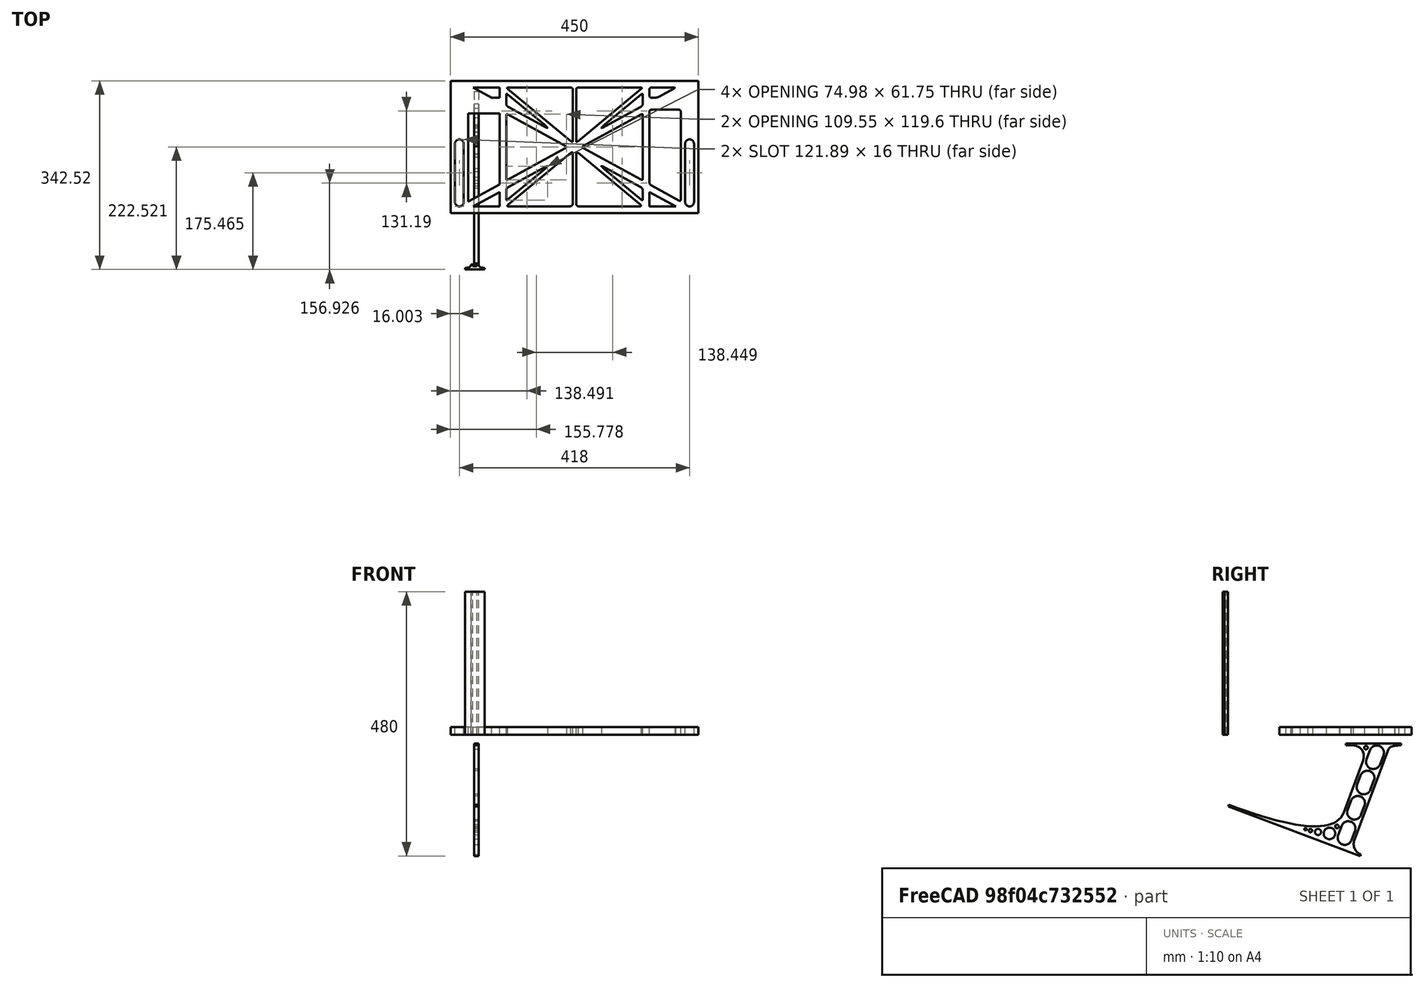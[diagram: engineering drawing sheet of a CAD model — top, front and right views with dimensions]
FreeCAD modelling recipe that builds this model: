
FCSTD DOCUMENT  (FreeCAD 0.19R0.19.2)
Label: laptopStand110
License: All rights reserved
LicenseURL: http://en.wikipedia.org/wiki/All_rights_reserved
objects: Sketcher::SketchObject×3, Part::Extrusion×3
note: 6 computed .brp shape members not serialized (recipe doc carries the construction recipe); baked Part::Feature solids carry a one-line shape summary decoded from their .brp

FEATURE [Sketcher::SketchObject] Sketch
  FullyConstrained = false
  sketch-geometry (298):
    g0: LineSegment StartX=-10.9272 StartY=-82.7794 StartZ=0 EndX=46.0728 EndY=-51.4823 EndZ=0
    g1: LineSegment StartX=-10.9272 StartY=77.3346 StartZ=0 EndX=-10.9272 EndY=-82.7794 EndZ=0
    g2: LineSegment StartX=-1.92719 StartY=-91.7794 StartZ=0 EndX=46.0728 EndY=-91.7794 EndZ=0
    g3: LineSegment StartX=318.073 StartY=-65.424 StartZ=0 EndX=318.073 EndY=-91.7794 EndZ=0
    g4: LineSegment StartX=318.073 StartY=-91.7794 StartZ=0 EndX=366.073 EndY=-91.7794 EndZ=0
    g5: LineSegment StartX=46.0728 StartY=-65.424 StartZ=0 EndX=-1.92719 EndY=-91.7794 EndZ=0
    g6: LineSegment StartX=46.0728 StartY=-65.424 StartZ=0 EndX=46.0728 EndY=-91.7794 EndZ=0
    g7: LineSegment StartX=46.0728 StartY=77.3346 StartZ=0 EndX=46.0728 EndY=-51.4823 EndZ=0
    g8: LineSegment StartX=-42.9272 StartY=136.221 StartZ=0 EndX=-42.9272 EndY=-103.779 EndZ=0
    g9: LineSegment StartX=407.073 StartY=136.221 StartZ=0 EndX=407.073 EndY=-103.779 EndZ=0
    g10: ArcOfCircle CenterX=-26.9272 CenterY=22.1087 CenterZ=0 NormalX=0 NormalY=0 NormalZ=1 AngleXU=0 Radius=8 StartAngle=1e-16 EndAngle=3.14159
    g11: ArcOfCircle CenterX=-26.9272 CenterY=-83.7794 CenterZ=0 NormalX=0 NormalY=0 NormalZ=1 AngleXU=0 Radius=8 StartAngle=3.14159 EndAngle=6.28319
    g12: LineSegment StartX=-34.9272 StartY=22.1087 StartZ=0 EndX=-34.9272 EndY=-83.7794 EndZ=0
    g13: LineSegment StartX=-18.9272 StartY=22.1087 StartZ=0 EndX=-18.9272 EndY=-83.7794 EndZ=0
    g14: ArcOfCircle CenterX=391.073 CenterY=22.1087 CenterZ=0 NormalX=0 NormalY=0 NormalZ=1 AngleXU=0 Radius=8 StartAngle=-4.4e-15 EndAngle=3.14159
    g15: LineSegment StartX=399.073 StartY=22.1087 StartZ=0 EndX=399.073 EndY=-83.7794 EndZ=0
    g16: LineSegment StartX=383.073 StartY=22.1087 StartZ=0 EndX=383.073 EndY=-83.7794 EndZ=0
    g17: ArcOfCircle CenterX=391.073 CenterY=-83.7794 CenterZ=0 NormalX=0 NormalY=0 NormalZ=1 AngleXU=0 Radius=8 StartAngle=3.14159 EndAngle=6.28319
    g18: Circle CenterX=175.022 CenterY=27.0628 CenterZ=0 NormalX=0 NormalY=0 NormalZ=1 AngleXU=0 Radius=1
    g19: Circle CenterX=179.022 CenterY=24.8665 CenterZ=0 NormalX=0 NormalY=0 NormalZ=1 AngleXU=0 Radius=1
    g20: Circle CenterX=179.022 CenterY=27.0628 CenterZ=0 NormalX=0 NormalY=0 NormalZ=1 AngleXU=0 Radius=1
    g21: BSplineCurve PolesCount=3 KnotsCount=2 Degree=2 IsPeriodic=0
    g22: GeomPoint X=175.022 Y=27.0628 Z=0
    g23: GeomPoint X=179.022 Y=27.0628 Z=0
    g24: Circle CenterX=189.124 CenterY=27.0628 CenterZ=0 NormalX=0 NormalY=0 NormalZ=1 AngleXU=0 Radius=1
    g25: Circle CenterX=185.124 CenterY=24.8665 CenterZ=0 NormalX=0 NormalY=0 NormalZ=1 AngleXU=0 Radius=1
    g26: Circle CenterX=185.124 CenterY=27.0628 CenterZ=0 NormalX=0 NormalY=0 NormalZ=1 AngleXU=0 Radius=1
    g27: BSplineCurve PolesCount=3 KnotsCount=2 Degree=2 IsPeriodic=0
    g28: GeomPoint X=189.124 Y=27.0628 Z=0
    g29: GeomPoint X=185.124 Y=27.0628 Z=0
    g30: Circle CenterX=175.022 CenterY=5.37834 CenterZ=0 NormalX=0 NormalY=0 NormalZ=1 AngleXU=0 Radius=1
    g31: Circle CenterX=179.022 CenterY=7.57463 CenterZ=0 NormalX=0 NormalY=0 NormalZ=1 AngleXU=0 Radius=1
    g32: Circle CenterX=179.022 CenterY=5.34704 CenterZ=0 NormalX=0 NormalY=0 NormalZ=1 AngleXU=0 Radius=1
    g33: BSplineCurve PolesCount=3 KnotsCount=2 Degree=2 IsPeriodic=0
    g34: GeomPoint X=175.022 Y=5.37834 Z=0
    g35: GeomPoint X=179.022 Y=5.34704 Z=0
    g36: Circle CenterX=189.124 CenterY=5.37834 CenterZ=0 NormalX=0 NormalY=0 NormalZ=1 AngleXU=0 Radius=1
    g37: Circle CenterX=185.124 CenterY=7.57463 CenterZ=0 NormalX=0 NormalY=0 NormalZ=1 AngleXU=0 Radius=1
    g38: Circle CenterX=185.124 CenterY=5.34704 CenterZ=0 NormalX=0 NormalY=0 NormalZ=1 AngleXU=0 Radius=1
    g39: BSplineCurve PolesCount=3 KnotsCount=2 Degree=2 IsPeriodic=0
    g40: GeomPoint X=189.124 Y=5.37834 Z=0
    g41: GeomPoint X=185.124 Y=5.34704 Z=0
    g42: Circle CenterX=165.871 CenterY=18.1458 CenterZ=0 NormalX=0 NormalY=0 NormalZ=1 AngleXU=0 Radius=1
    g43: Circle CenterX=169.377 CenterY=16.2206 CenterZ=0 NormalX=0 NormalY=0 NormalZ=1 AngleXU=0 Radius=1
    g44: Circle CenterX=165.871 CenterY=14.2954 CenterZ=0 NormalX=0 NormalY=0 NormalZ=1 AngleXU=0 Radius=1
    g45: BSplineCurve PolesCount=3 KnotsCount=2 Degree=2 IsPeriodic=0
    g46: GeomPoint X=165.871 Y=18.1458 Z=0
    g47: GeomPoint X=165.871 Y=14.2954 Z=0
    g48: Circle CenterX=198.275 CenterY=18.1458 CenterZ=0 NormalX=0 NormalY=0 NormalZ=1 AngleXU=0 Radius=1
    g49: Circle CenterX=194.768 CenterY=16.2206 CenterZ=0 NormalX=0 NormalY=0 NormalZ=1 AngleXU=0 Radius=1
    g50: Circle CenterX=198.275 CenterY=14.2954 CenterZ=0 NormalX=0 NormalY=0 NormalZ=1 AngleXU=0 Radius=1
    g51: BSplineCurve PolesCount=3 KnotsCount=2 Degree=2 IsPeriodic=0
    g52: GeomPoint X=198.275 Y=18.1458 Z=0
    g53: GeomPoint X=198.275 Y=14.2954 Z=0
    g54: LineSegment StartX=407.073 StartY=-103.779 StartZ=0 EndX=-42.9272 EndY=-103.779 EndZ=0
    g55: LineSegment StartX=407.073 StartY=136.221 StartZ=0 EndX=-42.9272 EndY=136.221 EndZ=0
    g56: LineSegment StartX=46.0728 StartY=77.3346 StartZ=0 EndX=-10.9272 EndY=77.3346 EndZ=0
    g57: LineSegment StartX=46.0728 StartY=105.865 StartZ=0 EndX=31.5028 EndY=105.865 EndZ=0
    g58: LineSegment StartX=46.0728 StartY=124.221 StartZ=0 EndX=46.0728 EndY=105.865 EndZ=0
    g59: LineSegment StartX=-1.92719 StartY=124.221 StartZ=0 EndX=31.5028 EndY=105.865 EndZ=0
    g60: LineSegment StartX=46.0728 StartY=124.221 StartZ=0 EndX=-1.92719 EndY=124.221 EndZ=0
    g61: Circle CenterX=125.607 CenterY=54.1951 CenterZ=0 NormalX=0 NormalY=0 NormalZ=1 AngleXU=0 Radius=1
    g62: Circle CenterX=139.632 CenterY=46.4944 CenterZ=0 NormalX=0 NormalY=0 NormalZ=1 AngleXU=0 Radius=1
    g63: Circle CenterX=127.326 CenterY=56.7187 CenterZ=0 NormalX=0 NormalY=0 NormalZ=1 AngleXU=0 Radius=1
    g64: BSplineCurve PolesCount=3 KnotsCount=2 Degree=2 IsPeriodic=0
    g65: GeomPoint X=125.607 Y=54.1951 Z=0
    g66: GeomPoint X=127.326 Y=56.7187 Z=0
    g67: Circle CenterX=236.821 CenterY=56.7187 CenterZ=0 NormalX=0 NormalY=0 NormalZ=1 AngleXU=0 Radius=1
    g68: Circle CenterX=224.513 CenterY=46.4944 CenterZ=0 NormalX=0 NormalY=0 NormalZ=1 AngleXU=0 Radius=1
    g69: Circle CenterX=238.538 CenterY=54.1951 CenterZ=0 NormalX=0 NormalY=0 NormalZ=1 AngleXU=0 Radius=1
    g70: BSplineCurve PolesCount=3 KnotsCount=2 Degree=2 IsPeriodic=0
    g71: GeomPoint X=236.821 Y=56.7187 Z=0
    g72: GeomPoint X=238.538 Y=54.1951 Z=0
    g73: Circle CenterX=238.538 CenterY=-21.7539 CenterZ=0 NormalX=0 NormalY=0 NormalZ=1 AngleXU=0 Radius=1
    g74: Circle CenterX=224.513 CenterY=-14.0532 CenterZ=0 NormalX=0 NormalY=0 NormalZ=1 AngleXU=0 Radius=1
    g75: Circle CenterX=236.821 CenterY=-24.2775 CenterZ=0 NormalX=0 NormalY=0 NormalZ=1 AngleXU=0 Radius=1
    g76: BSplineCurve PolesCount=3 KnotsCount=2 Degree=2 IsPeriodic=0
    g77: GeomPoint X=238.538 Y=-21.7539 Z=0
    g78: GeomPoint X=236.821 Y=-24.2775 Z=0
    g79: Circle CenterX=125.607 CenterY=-21.7539 CenterZ=0 NormalX=0 NormalY=0 NormalZ=1 AngleXU=0 Radius=1
    g80: Circle CenterX=139.632 CenterY=-14.0532 CenterZ=0 NormalX=0 NormalY=0 NormalZ=1 AngleXU=0 Radius=1
    g81: Circle CenterX=127.325 CenterY=-24.2775 CenterZ=0 NormalX=0 NormalY=0 NormalZ=1 AngleXU=0 Radius=1
    g82: BSplineCurve PolesCount=3 KnotsCount=2 Degree=2 IsPeriodic=0
    g83: GeomPoint X=125.607 Y=-21.7539 Z=0
    g84: GeomPoint X=127.325 Y=-24.2775 Z=0
    g85: Circle CenterX=302.996 CenterY=111.695 CenterZ=0 NormalX=0 NormalY=0 NormalZ=1 AngleXU=0 Radius=1
    g86: Circle CenterX=306.073 CenterY=114.251 CenterZ=0 NormalX=0 NormalY=0 NormalZ=1 AngleXU=0 Radius=1
    g87: Circle CenterX=306.073 CenterY=110.251 CenterZ=0 NormalX=0 NormalY=0 NormalZ=1 AngleXU=0 Radius=1
    g88: BSplineCurve PolesCount=3 KnotsCount=2 Degree=2 IsPeriodic=0
    g89: GeomPoint X=302.996 Y=111.695 Z=0
    g90: GeomPoint X=306.073 Y=110.251 Z=0
    g91: Circle CenterX=306.073 CenterY=95.2763 CenterZ=0 NormalX=0 NormalY=0 NormalZ=1 AngleXU=0 Radius=1
    g92: Circle CenterX=306.073 CenterY=91.2763 CenterZ=0 NormalX=0 NormalY=0 NormalZ=1 AngleXU=0 Radius=1
    g93: Circle CenterX=302.567 CenterY=89.3511 CenterZ=0 NormalX=0 NormalY=0 NormalZ=1 AngleXU=0 Radius=1
    g94: BSplineCurve PolesCount=3 KnotsCount=2 Degree=2 IsPeriodic=0
    g95: GeomPoint X=306.073 Y=95.2763 Z=0
    g96: GeomPoint X=302.567 Y=89.3511 Z=0
    g97: LineSegment StartX=306.073 StartY=110.251 StartZ=0 EndX=306.073 EndY=95.2763 EndZ=0
    g98: LineSegment StartX=302.996 StartY=111.695 StartZ=0 EndX=236.821 EndY=56.7187 EndZ=0
    g99: LineSegment StartX=238.538 StartY=54.1951 StartZ=0 EndX=302.567 EndY=89.3511 EndZ=0
    g100: Circle CenterX=61.1496 CenterY=111.695 CenterZ=0 NormalX=0 NormalY=0 NormalZ=1 AngleXU=0 Radius=1
    g101: Circle CenterX=58.0728 CenterY=114.251 CenterZ=0 NormalX=0 NormalY=0 NormalZ=1 AngleXU=0 Radius=1
    g102: Circle CenterX=58.0728 CenterY=110.251 CenterZ=0 NormalX=0 NormalY=0 NormalZ=1 AngleXU=0 Radius=1
    g103: BSplineCurve PolesCount=3 KnotsCount=2 Degree=2 IsPeriodic=0
    g104: GeomPoint X=61.1496 Y=111.695 Z=0
    g105: GeomPoint X=58.0728 Y=110.251 Z=0
    g106: Circle CenterX=61.5791 CenterY=89.3511 CenterZ=0 NormalX=0 NormalY=0 NormalZ=1 AngleXU=0 Radius=1
    g107: Circle CenterX=58.0728 CenterY=91.2763 CenterZ=0 NormalX=0 NormalY=0 NormalZ=1 AngleXU=0 Radius=1
    g108: Circle CenterX=58.0728 CenterY=95.2763 CenterZ=0 NormalX=0 NormalY=0 NormalZ=1 AngleXU=0 Radius=1
    g109: BSplineCurve PolesCount=3 KnotsCount=2 Degree=2 IsPeriodic=0
    g110: GeomPoint X=61.5791 Y=89.3511 Z=0
    g111: GeomPoint X=58.0728 Y=95.2763 Z=0
    g112: LineSegment StartX=58.0728 StartY=110.251 StartZ=0 EndX=58.0728 EndY=95.2763 EndZ=0
    g113: LineSegment StartX=61.1496 StartY=111.695 StartZ=0 EndX=127.326 EndY=56.7187 EndZ=0
    g114: LineSegment StartX=125.607 StartY=54.1951 StartZ=0 EndX=61.5791 EndY=89.3511 EndZ=0
    g115: Circle CenterX=61.5791 CenterY=-56.9099 CenterZ=0 NormalX=0 NormalY=0 NormalZ=1 AngleXU=0 Radius=1
    g116: Circle CenterX=58.0728 CenterY=-58.8351 CenterZ=0 NormalX=0 NormalY=0 NormalZ=1 AngleXU=0 Radius=1
    g117: Circle CenterX=58.0728 CenterY=-62.8351 CenterZ=0 NormalX=0 NormalY=0 NormalZ=1 AngleXU=0 Radius=1
    g118: BSplineCurve PolesCount=3 KnotsCount=2 Degree=2 IsPeriodic=0
    g119: GeomPoint X=61.5791 Y=-56.9099 Z=0
    g120: GeomPoint X=58.0728 Y=-62.8351 Z=0
    g121: Circle CenterX=58.0728 CenterY=-77.8102 CenterZ=0 NormalX=0 NormalY=0 NormalZ=1 AngleXU=0 Radius=1
    g122: Circle CenterX=58.0728 CenterY=-81.8102 CenterZ=0 NormalX=0 NormalY=0 NormalZ=1 AngleXU=0 Radius=1
    g123: Circle CenterX=61.1496 CenterY=-79.2541 CenterZ=0 NormalX=0 NormalY=0 NormalZ=1 AngleXU=0 Radius=1
    g124: BSplineCurve PolesCount=3 KnotsCount=2 Degree=2 IsPeriodic=0
    g125: GeomPoint X=58.0728 Y=-77.8102 Z=0
    g126: GeomPoint X=61.1496 Y=-79.2541 Z=0
    g127: LineSegment StartX=58.0728 StartY=-62.8351 StartZ=0 EndX=58.0728 EndY=-77.8102 EndZ=0
    g128: LineSegment StartX=61.1496 StartY=-79.2541 StartZ=0 EndX=127.325 EndY=-24.2775 EndZ=0
    g129: LineSegment StartX=125.607 StartY=-21.7539 StartZ=0 EndX=61.5791 EndY=-56.9099 EndZ=0
    g130: Circle CenterX=302.567 CenterY=-56.9099 CenterZ=0 NormalX=0 NormalY=0 NormalZ=1 AngleXU=0 Radius=1
    g131: Circle CenterX=306.073 CenterY=-58.8351 CenterZ=0 NormalX=0 NormalY=0 NormalZ=1 AngleXU=0 Radius=1
    g132: Circle CenterX=306.073 CenterY=-62.8351 CenterZ=0 NormalX=0 NormalY=0 NormalZ=1 AngleXU=0 Radius=1
    g133: BSplineCurve PolesCount=3 KnotsCount=2 Degree=2 IsPeriodic=0
    g134: GeomPoint X=302.567 Y=-56.9099 Z=0
    g135: GeomPoint X=306.073 Y=-62.8351 Z=0
    g136: Circle CenterX=302.996 CenterY=-79.2541 CenterZ=0 NormalX=0 NormalY=0 NormalZ=1 AngleXU=0 Radius=1
    g137: Circle CenterX=306.073 CenterY=-81.8102 CenterZ=0 NormalX=0 NormalY=0 NormalZ=1 AngleXU=0 Radius=1
    g138: Circle CenterX=306.073 CenterY=-77.8102 CenterZ=0 NormalX=0 NormalY=0 NormalZ=1 AngleXU=0 Radius=1
    g139: BSplineCurve PolesCount=3 KnotsCount=2 Degree=2 IsPeriodic=0
    g140: GeomPoint X=302.996 Y=-79.2541 Z=0
    g141: GeomPoint X=306.073 Y=-77.8102 Z=0
    g142: LineSegment StartX=306.073 StartY=-62.8351 StartZ=0 EndX=306.073 EndY=-77.8102 EndZ=0
    g143: LineSegment StartX=302.996 StartY=-79.2541 StartZ=0 EndX=236.821 EndY=-24.2775 EndZ=0
    g144: LineSegment StartX=238.538 StartY=-21.7539 StartZ=0 EndX=302.567 EndY=-56.9099 EndZ=0
    g145: Circle CenterX=61.6457 CenterY=-88.8112 CenterZ=0 NormalX=0 NormalY=0 NormalZ=1 AngleXU=0 Radius=1
    g146: Circle CenterX=58.0728 CenterY=-91.7794 CenterZ=0 NormalX=0 NormalY=0 NormalZ=1 AngleXU=0 Radius=1
    g147: Circle CenterX=63.9135 CenterY=-91.7794 CenterZ=0 NormalX=0 NormalY=0 NormalZ=1 AngleXU=0 Radius=1
    g148: BSplineCurve PolesCount=3 KnotsCount=2 Degree=2 IsPeriodic=0
    g149: GeomPoint X=61.6457 Y=-88.8112 Z=0
    g150: GeomPoint X=63.9135 Y=-91.7794 Z=0
    g151: Circle CenterX=179.022 CenterY=-85.8163 CenterZ=0 NormalX=0 NormalY=0 NormalZ=1 AngleXU=0 Radius=1
    g152: Circle CenterX=179.022 CenterY=-91.7794 CenterZ=0 NormalX=0 NormalY=0 NormalZ=1 AngleXU=0 Radius=1
    g153: Circle CenterX=171.895 CenterY=-91.7794 CenterZ=0 NormalX=0 NormalY=0 NormalZ=1 AngleXU=0 Radius=1
    g154: BSplineCurve PolesCount=3 KnotsCount=2 Degree=2 IsPeriodic=0
    g155: GeomPoint X=179.022 Y=-85.8163 Z=0
    g156: GeomPoint X=171.895 Y=-91.7794 Z=0
    g157: Circle CenterX=185.124 CenterY=-86.2028 CenterZ=0 NormalX=0 NormalY=0 NormalZ=1 AngleXU=0 Radius=1
    g158: Circle CenterX=185.124 CenterY=-91.7794 CenterZ=0 NormalX=0 NormalY=0 NormalZ=1 AngleXU=0 Radius=1
    g159: Circle CenterX=191.747 CenterY=-91.7794 CenterZ=0 NormalX=0 NormalY=0 NormalZ=1 AngleXU=0 Radius=1
    g160: BSplineCurve PolesCount=3 KnotsCount=2 Degree=2 IsPeriodic=0
    g161: GeomPoint X=185.124 Y=-86.2028 Z=0
    g162: GeomPoint X=191.747 Y=-91.7794 Z=0
    g163: Circle CenterX=299.888 CenterY=-86.6413 CenterZ=0 NormalX=0 NormalY=0 NormalZ=1 AngleXU=0 Radius=1
    g164: Circle CenterX=306.073 CenterY=-91.7794 CenterZ=0 NormalX=0 NormalY=0 NormalZ=1 AngleXU=0 Radius=1
    g165: Circle CenterX=298.776 CenterY=-91.7794 CenterZ=0 NormalX=0 NormalY=0 NormalZ=1 AngleXU=0 Radius=1
    g166: BSplineCurve PolesCount=3 KnotsCount=2 Degree=2 IsPeriodic=0
    g167: GeomPoint X=299.888 Y=-86.6413 Z=0
    g168: GeomPoint X=298.776 Y=-91.7794 Z=0
    g169: LineSegment StartX=189.124 StartY=5.37834 StartZ=0 EndX=299.888 EndY=-86.6413 EndZ=0
    g170: LineSegment StartX=298.776 StartY=-91.7794 StartZ=0 EndX=191.747 EndY=-91.7794 EndZ=0
    g171: LineSegment StartX=185.124 StartY=-86.2028 StartZ=0 EndX=185.124 EndY=5.34704 EndZ=0
    g172: LineSegment StartX=179.022 StartY=5.34704 StartZ=0 EndX=179.022 EndY=-85.8163 EndZ=0
    g173: LineSegment StartX=171.895 StartY=-91.7794 StartZ=0 EndX=63.9135 EndY=-91.7794 EndZ=0
    g174: LineSegment StartX=61.6457 StartY=-88.8112 StartZ=0 EndX=175.022 EndY=5.37834 EndZ=0
    g175: Circle CenterX=302.073 CenterY=124.221 CenterZ=0 NormalX=0 NormalY=0 NormalZ=1 AngleXU=0 Radius=1
    g176: Circle CenterX=306.073 CenterY=124.221 CenterZ=0 NormalX=0 NormalY=0 NormalZ=1 AngleXU=0 Radius=1
    g177: Circle CenterX=302.996 CenterY=121.665 CenterZ=0 NormalX=0 NormalY=0 NormalZ=1 AngleXU=0 Radius=1
    g178: BSplineCurve PolesCount=3 KnotsCount=2 Degree=2 IsPeriodic=0
    g179: GeomPoint X=302.073 Y=124.221 Z=0
    g180: GeomPoint X=302.996 Y=121.665 Z=0
    g181: Circle CenterX=189.124 CenterY=124.221 CenterZ=0 NormalX=0 NormalY=0 NormalZ=1 AngleXU=0 Radius=1
    g182: Circle CenterX=185.124 CenterY=124.221 CenterZ=0 NormalX=0 NormalY=0 NormalZ=1 AngleXU=0 Radius=1
    g183: Circle CenterX=185.124 CenterY=120.221 CenterZ=0 NormalX=0 NormalY=0 NormalZ=1 AngleXU=0 Radius=1
    g184: BSplineCurve PolesCount=3 KnotsCount=2 Degree=2 IsPeriodic=0
    g185: GeomPoint X=189.124 Y=124.221 Z=0
    g186: GeomPoint X=185.124 Y=120.221 Z=0
    g187: Circle CenterX=175.022 CenterY=124.221 CenterZ=0 NormalX=0 NormalY=0 NormalZ=1 AngleXU=0 Radius=1
    g188: Circle CenterX=179.022 CenterY=124.221 CenterZ=0 NormalX=0 NormalY=0 NormalZ=1 AngleXU=0 Radius=1
    g189: Circle CenterX=179.022 CenterY=120.221 CenterZ=0 NormalX=0 NormalY=0 NormalZ=1 AngleXU=0 Radius=1
    g190: BSplineCurve PolesCount=3 KnotsCount=2 Degree=2 IsPeriodic=0
    g191: GeomPoint X=175.022 Y=124.221 Z=0
    g192: GeomPoint X=179.022 Y=120.221 Z=0
    g193: Circle CenterX=62.0728 CenterY=124.221 CenterZ=0 NormalX=0 NormalY=0 NormalZ=1 AngleXU=0 Radius=1
    g194: Circle CenterX=58.0728 CenterY=124.221 CenterZ=0 NormalX=0 NormalY=0 NormalZ=1 AngleXU=0 Radius=1
    g195: Circle CenterX=61.1496 CenterY=121.665 CenterZ=0 NormalX=0 NormalY=0 NormalZ=1 AngleXU=0 Radius=1
    g196: BSplineCurve PolesCount=3 KnotsCount=2 Degree=2 IsPeriodic=0
    g197: GeomPoint X=62.0728 Y=124.221 Z=0
    g198: GeomPoint X=61.1496 Y=121.665 Z=0
    g199: LineSegment StartX=62.0728 StartY=124.221 StartZ=0 EndX=175.022 EndY=124.221 EndZ=0
    g200: LineSegment StartX=179.022 StartY=120.221 StartZ=0 EndX=179.022 EndY=27.0628 EndZ=0
    g201: LineSegment StartX=185.124 StartY=27.0628 StartZ=0 EndX=185.124 EndY=120.221 EndZ=0
    g202: LineSegment StartX=189.124 StartY=124.221 StartZ=0 EndX=302.073 EndY=124.221 EndZ=0
    g203: LineSegment StartX=302.996 StartY=121.665 StartZ=0 EndX=189.124 EndY=27.0628 EndZ=0
    g204: LineSegment StartX=175.022 StartY=27.0628 StartZ=0 EndX=61.1496 EndY=121.665 EndZ=0
    g205: Circle CenterX=61.5791 CenterY=75.4095 CenterZ=0 NormalX=0 NormalY=0 NormalZ=1 AngleXU=0 Radius=1
    g206: Circle CenterX=58.0728 CenterY=77.3346 CenterZ=0 NormalX=0 NormalY=0 NormalZ=1 AngleXU=0 Radius=1
    g207: Circle CenterX=58.0728 CenterY=73.3346 CenterZ=0 NormalX=0 NormalY=0 NormalZ=1 AngleXU=0 Radius=1
    g208: BSplineCurve PolesCount=3 KnotsCount=2 Degree=2 IsPeriodic=0
    g209: GeomPoint X=61.5791 Y=75.4095 Z=0
    g210: GeomPoint X=58.0728 Y=73.3346 Z=0
    g211: Circle CenterX=58.0728 CenterY=-40.8935 CenterZ=0 NormalX=0 NormalY=0 NormalZ=1 AngleXU=0 Radius=1
    g212: Circle CenterX=58.0728 CenterY=-44.8935 CenterZ=0 NormalX=0 NormalY=0 NormalZ=1 AngleXU=0 Radius=1
    g213: Circle CenterX=61.5791 CenterY=-42.9683 CenterZ=0 NormalX=0 NormalY=0 NormalZ=1 AngleXU=0 Radius=1
    g214: BSplineCurve PolesCount=3 KnotsCount=2 Degree=2 IsPeriodic=0
    g215: GeomPoint X=58.0728 Y=-40.8935 Z=0
    g216: GeomPoint X=61.5791 Y=-42.9683 Z=0
    g217: LineSegment StartX=61.5791 StartY=-42.9683 StartZ=0 EndX=165.871 EndY=14.2954 EndZ=0
    g218: LineSegment StartX=165.871 StartY=18.1458 StartZ=0 EndX=61.5791 EndY=75.4095 EndZ=0
    g219: LineSegment StartX=58.0728 StartY=73.3346 StartZ=0 EndX=58.0728 EndY=-40.8935 EndZ=0
    g220: Circle CenterX=302.567 CenterY=-42.9683 CenterZ=0 NormalX=0 NormalY=0 NormalZ=1 AngleXU=0 Radius=1
    g221: Circle CenterX=306.073 CenterY=-44.8935 CenterZ=0 NormalX=0 NormalY=0 NormalZ=1 AngleXU=0 Radius=1
    g222: Circle CenterX=306.073 CenterY=-40.8935 CenterZ=0 NormalX=0 NormalY=0 NormalZ=1 AngleXU=0 Radius=1
    g223: BSplineCurve PolesCount=3 KnotsCount=2 Degree=2 IsPeriodic=0
    g224: GeomPoint X=302.567 Y=-42.9683 Z=0
    g225: GeomPoint X=306.073 Y=-40.8935 Z=0
    g226: Circle CenterX=306.073 CenterY=73.3346 CenterZ=0 NormalX=0 NormalY=0 NormalZ=1 AngleXU=0 Radius=1
    g227: Circle CenterX=306.073 CenterY=77.3346 CenterZ=0 NormalX=0 NormalY=0 NormalZ=1 AngleXU=0 Radius=1
    g228: Circle CenterX=302.567 CenterY=75.4095 CenterZ=0 NormalX=0 NormalY=0 NormalZ=1 AngleXU=0 Radius=1
    g229: BSplineCurve PolesCount=3 KnotsCount=2 Degree=2 IsPeriodic=0
    g230: GeomPoint X=306.073 Y=73.3346 Z=0
    g231: GeomPoint X=302.567 Y=75.4095 Z=0
    g232: LineSegment StartX=302.567 StartY=-42.9683 StartZ=0 EndX=198.275 EndY=14.2954 EndZ=0
    g233: LineSegment StartX=198.275 StartY=18.1458 StartZ=0 EndX=302.567 EndY=75.4095 EndZ=0
    g234: LineSegment StartX=306.073 StartY=73.3346 StartZ=0 EndX=306.073 EndY=-40.8935 EndZ=0
    g235: LineSegment StartX=322.073 StartY=105.865 StartZ=0 EndX=328.643 EndY=105.865 EndZ=0
    g236: LineSegment StartX=318.073 StartY=120.221 StartZ=0 EndX=318.073 EndY=109.865 EndZ=0
    g237: LineSegment StartX=336.157 StartY=107.779 StartZ=0 EndX=362.567 EndY=122.294 EndZ=0
    g238: Circle CenterX=362.073 CenterY=124.221 CenterZ=0 NormalX=0 NormalY=0 NormalZ=1 AngleXU=0 Radius=1
    g239: Circle CenterX=366.073 CenterY=124.221 CenterZ=0 NormalX=0 NormalY=0 NormalZ=1 AngleXU=0 Radius=1
    g240: Circle CenterX=362.567 CenterY=122.294 CenterZ=0 NormalX=0 NormalY=0 NormalZ=1 AngleXU=0 Radius=1
    g241: BSplineCurve PolesCount=3 KnotsCount=2 Degree=2 IsPeriodic=0
    g242: GeomPoint X=362.073 Y=124.221 Z=0
    g243: GeomPoint X=362.567 Y=122.294 Z=0
    g244: Circle CenterX=322.073 CenterY=124.221 CenterZ=0 NormalX=0 NormalY=0 NormalZ=1 AngleXU=0 Radius=1
    g245: Circle CenterX=318.073 CenterY=124.221 CenterZ=0 NormalX=0 NormalY=0 NormalZ=1 AngleXU=0 Radius=1
    g246: Circle CenterX=318.073 CenterY=120.221 CenterZ=0 NormalX=0 NormalY=0 NormalZ=1 AngleXU=0 Radius=1
    g247: BSplineCurve PolesCount=3 KnotsCount=2 Degree=2 IsPeriodic=0
    g248: GeomPoint X=322.073 Y=124.221 Z=0
    g249: GeomPoint X=318.073 Y=120.221 Z=0
    g250: Circle CenterX=322.073 CenterY=105.865 CenterZ=0 NormalX=0 NormalY=0 NormalZ=1 AngleXU=0 Radius=1
    g251: Circle CenterX=318.073 CenterY=105.865 CenterZ=0 NormalX=0 NormalY=0 NormalZ=1 AngleXU=0 Radius=1
    g252: Circle CenterX=318.073 CenterY=109.865 CenterZ=0 NormalX=0 NormalY=0 NormalZ=1 AngleXU=0 Radius=1
    g253: BSplineCurve PolesCount=3 KnotsCount=2 Degree=2 IsPeriodic=0
    g254: GeomPoint X=322.073 Y=105.865 Z=0
    g255: GeomPoint X=318.073 Y=109.865 Z=0
    g256: Circle CenterX=336.157 CenterY=107.779 CenterZ=0 NormalX=0 NormalY=0 NormalZ=1 AngleXU=0 Radius=1
    g257: Circle CenterX=332.651 CenterY=105.853 CenterZ=0 NormalX=0 NormalY=0 NormalZ=1 AngleXU=0 Radius=1
    g258: Circle CenterX=328.643 CenterY=105.865 CenterZ=0 NormalX=0 NormalY=0 NormalZ=1 AngleXU=0 Radius=1
    g259: BSplineCurve PolesCount=3 KnotsCount=2 Degree=2 IsPeriodic=0
    g260: GeomPoint X=336.157 Y=107.779 Z=0
    g261: GeomPoint X=328.643 Y=105.865 Z=0
    g262: LineSegment StartX=322.073 StartY=124.221 StartZ=0 EndX=362.073 EndY=124.221 EndZ=0
    g263: Circle CenterX=371.567 CenterY=-80.8644 CenterZ=0 NormalX=0 NormalY=0 NormalZ=1 AngleXU=0 Radius=1
    g264: Circle CenterX=375.073 CenterY=-82.7896 CenterZ=0 NormalX=0 NormalY=0 NormalZ=1 AngleXU=0 Radius=1
    g265: Circle CenterX=375.073 CenterY=-78.7896 CenterZ=0 NormalX=0 NormalY=0 NormalZ=1 AngleXU=0 Radius=1
    g266: BSplineCurve PolesCount=3 KnotsCount=2 Degree=2 IsPeriodic=0
    g267: GeomPoint X=371.567 Y=-80.8644 Z=0
    g268: GeomPoint X=375.073 Y=-78.7896 Z=0
    g269: Circle CenterX=321.579 CenterY=-53.4075 CenterZ=0 NormalX=0 NormalY=0 NormalZ=1 AngleXU=0 Radius=1
    g270: Circle CenterX=318.073 CenterY=-51.4823 CenterZ=0 NormalX=0 NormalY=0 NormalZ=1 AngleXU=0 Radius=1
    g271: Circle CenterX=318.073 CenterY=-47.4823 CenterZ=0 NormalX=0 NormalY=0 NormalZ=1 AngleXU=0 Radius=1
    g272: BSplineCurve PolesCount=3 KnotsCount=2 Degree=2 IsPeriodic=0
    g273: GeomPoint X=321.579 Y=-53.4075 Z=0
    g274: GeomPoint X=318.073 Y=-47.4823 Z=0
    g275: Circle CenterX=318.073 CenterY=79.9235 CenterZ=0 NormalX=0 NormalY=0 NormalZ=1 AngleXU=0 Radius=1
    g276: Circle CenterX=318.073 CenterY=83.9235 CenterZ=0 NormalX=0 NormalY=0 NormalZ=1 AngleXU=0 Radius=1
    g277: Circle CenterX=322.073 CenterY=83.9235 CenterZ=0 NormalX=0 NormalY=0 NormalZ=1 AngleXU=0 Radius=1
    g278: BSplineCurve PolesCount=3 KnotsCount=2 Degree=2 IsPeriodic=0
    g279: GeomPoint X=318.073 Y=79.9235 Z=0
    g280: GeomPoint X=322.073 Y=83.9235 Z=0
    g281: Circle CenterX=375.073 CenterY=79.9235 CenterZ=0 NormalX=0 NormalY=0 NormalZ=1 AngleXU=0 Radius=1
    g282: Circle CenterX=375.073 CenterY=83.9235 CenterZ=0 NormalX=0 NormalY=0 NormalZ=1 AngleXU=0 Radius=1
    g283: Circle CenterX=371.073 CenterY=83.9235 CenterZ=0 NormalX=0 NormalY=0 NormalZ=1 AngleXU=0 Radius=1
    g284: BSplineCurve PolesCount=3 KnotsCount=2 Degree=2 IsPeriodic=0
    g285: GeomPoint X=375.073 Y=79.9235 Z=0
    g286: GeomPoint X=371.073 Y=83.9235 Z=0
    g287: LineSegment StartX=322.073 StartY=83.9235 StartZ=0 EndX=371.073 EndY=83.9235 EndZ=0
    g288: LineSegment StartX=375.073 StartY=79.9235 StartZ=0 EndX=375.073 EndY=-78.7896 EndZ=0
    g289: LineSegment StartX=371.567 StartY=-80.8644 StartZ=0 EndX=321.579 EndY=-53.4075 EndZ=0
    g290: LineSegment StartX=318.073 StartY=-47.4823 StartZ=0 EndX=318.073 EndY=79.9235 EndZ=0
    g291: LineSegment StartX=318.073 StartY=-65.424 StartZ=0 EndX=321.549 EndY=-67.4026 EndZ=0
    g292: LineSegment StartX=366.073 StartY=-91.7794 StartZ=0 EndX=362.567 EndY=-89.8542 EndZ=0
    g293: LineSegment StartX=366.073 StartY=-91.7794 StartZ=0 EndX=362.073 EndY=-91.7794 EndZ=0
    g294: LineSegment StartX=318.073 StartY=-91.7794 StartZ=0 EndX=322.073 EndY=-91.7794 EndZ=0
    g295: LineSegment StartX=318.073 StartY=-91.7794 StartZ=0 EndX=318.073 EndY=-87.7794 EndZ=0
    g296: LineSegment StartX=318.073 StartY=-65.424 StartZ=0 EndX=318.073 EndY=-69.424 EndZ=0
    g297: LineSegment StartX=318.073 StartY=-65.424 StartZ=0 EndX=366.073 EndY=-91.7794 EndZ=0
  constraints (505):
    c: Horizontal(g2)
    c: Coincident(g6,g5)
    c: Coincident(g0,g7)
    c: Block(g3)
    c: Block(g6)
    c: Block(g5)
    c: Block(g0)
    c: Block(g1)
    c: Block(g4)
    c: Block(g2)
    c: Vertical(g8)
    c: Vertical(g9)
    c: Block(g9)
    c: Block(g8)
    c: Tangent(g10,g13) = 1.5708
    c: Tangent(g10,g12) = -1.5708
    c: Tangent(g12,g11) = -1.5708
    c: Tangent(g13,g11) = 1.5708
    c: Vertical(g12)
    c: Equal(g10,g11)
    c: Block(g13)
    c: Block(g12)
    c: Tangent(g14,g15) = 1.5708
    c: Tangent(g15,g17) = 1.5708
    c: Equal(g14,g17)
    c: Coincident(g16,g14)
    c: Coincident(g16,g17)
    c: Block(g15)
    c: Block(g16)
    c: Weight(g18) = 1
    c: Equal(g18,g19)
    c: Equal(g18,g20)
    c: InternalAlignment(g18,g21)
    c: InternalAlignment(g19,g21)
    c: InternalAlignment(g20,g21)
    c: InternalAlignment(g22,g21)
    c: InternalAlignment(g23,g21)
    c: Weight(g24) = 1
    c: Equal(g24,g25)
    c: Equal(g24,g26)
    c: InternalAlignment(g24,g27)
    c: InternalAlignment(g25,g27)
    c: InternalAlignment(g26,g27)
    c: InternalAlignment(g28,g27)
    c: InternalAlignment(g29,g27)
    c: Block(g27)
    c: Block(g21)
    c: Weight(g30) = 1
    c: Equal(g30,g31)
    c: Equal(g30,g32)
    c: InternalAlignment(g30,g33)
    c: InternalAlignment(g31,g33)
    c: InternalAlignment(g32,g33)
    c: InternalAlignment(g34,g33)
    c: InternalAlignment(g35,g33)
    c: Weight(g36) = 1
    c: Equal(g36,g37)
    c: Equal(g36,g38)
    c: InternalAlignment(g36,g39)
    c: InternalAlignment(g37,g39)
    c: InternalAlignment(g38,g39)
    c: InternalAlignment(g40,g39)
    c: InternalAlignment(g41,g39)
    c: Block(g39)
    c: Block(g33)
    c: Weight(g42) = 1
    c: Equal(g42,g43)
    c: Equal(g42,g44)
    c: InternalAlignment(g42,g45)
    c: InternalAlignment(g43,g45)
    c: InternalAlignment(g44,g45)
    c: InternalAlignment(g46,g45)
    c: InternalAlignment(g47,g45)
    c: Weight(g48) = 1
    c: Equal(g48,g49)
    c: Equal(g48,g50)
    c: InternalAlignment(g48,g51)
    c: InternalAlignment(g49,g51)
    c: InternalAlignment(g50,g51)
    c: InternalAlignment(g52,g51)
    c: InternalAlignment(g53,g51)
    c: Block(g45)
    c: Block(g51)
    c: Coincident(g54,g9)
    c: Coincident(g54,g8)
    c: Horizontal(g54)
    c: Distance(g54) = 450
    c: Coincident(g55,g9)
    c: Coincident(g55,g8)
    c: Horizontal(g55)
    c: Horizontal(g56)
    c: Coincident(g7,g56)
    c: Horizontal(g57)
    c: Vertical(g58)
    c: Block(g58)
    c: Block(g57)
    c: Block(g56)
    c: Distance(g58) = 18.3554
    c: Coincident(g60,g58)
    c: Coincident(g60,g59)
    c: Horizontal(g60)
    c: Block(g60)
    c: Block(g59)
    c: Coincident(g57,g59)
    c: Coincident(g1,g56)
    c: Weight(g61) = 1
    c: Equal(g61,g62)
    c: Equal(g61,g63)
    c: InternalAlignment(g61,g64)
    c: InternalAlignment(g62,g64)
    c: InternalAlignment(g63,g64)
    c: InternalAlignment(g65,g64)
    c: InternalAlignment(g66,g64)
    c: Block(g64)
    c: Weight(g67) = 1
    c: Equal(g67,g68)
    c: Equal(g67,g69)
    c: InternalAlignment(g67,g70)
    c: InternalAlignment(g68,g70)
    c: InternalAlignment(g69,g70)
    c: InternalAlignment(g71,g70)
    c: InternalAlignment(g72,g70)
    c: Block(g70)
    c: Weight(g73) = 1
    c: Equal(g73,g74)
    c: Equal(g73,g75)
    c: InternalAlignment(g73,g76)
    c: InternalAlignment(g74,g76)
    c: InternalAlignment(g75,g76)
    c: InternalAlignment(g77,g76)
    c: InternalAlignment(g78,g76)
    c: Block(g76)
    c: Weight(g79) = 1
    c: Equal(g79,g80)
    c: Equal(g79,g81)
    c: InternalAlignment(g79,g82)
    c: InternalAlignment(g80,g82)
    c: InternalAlignment(g81,g82)
    c: InternalAlignment(g83,g82)
    c: InternalAlignment(g84,g82)
    c: Block(g82)
    c: Weight(g85) = 1
    c: Equal(g85,g86)
    c: Equal(g85,g87)
    c: InternalAlignment(g85,g88)
    c: InternalAlignment(g86,g88)
    c: InternalAlignment(g87,g88)
    c: InternalAlignment(g89,g88)
    c: InternalAlignment(g90,g88)
    c: Weight(g91) = 1
    c: Equal(g91,g92)
    c: Equal(g91,g93)
    c: InternalAlignment(g91,g94)
    c: InternalAlignment(g92,g94)
    c: InternalAlignment(g93,g94)
    c: InternalAlignment(g95,g94)
    c: InternalAlignment(g96,g94)
    c: Block(g88)
    c: Block(g94)
    c: Coincident(g97,g88)
    c: Coincident(g97,g94)
    c: Vertical(g97)
    c: Coincident(g98,g88)
    c: Coincident(g98,g70)
    c: Coincident(g99,g70)
    c: Coincident(g99,g94)
    c: Weight(g100) = 1
    c: Equal(g100,g101)
    c: Equal(g100,g102)
    c: InternalAlignment(g100,g103)
    c: InternalAlignment(g101,g103)
    c: InternalAlignment(g102,g103)
    c: InternalAlignment(g104,g103)
    c: InternalAlignment(g105,g103)
    c: Weight(g106) = 1
    c: Equal(g106,g107)
    c: Equal(g106,g108)
    c: InternalAlignment(g106,g109)
    c: InternalAlignment(g107,g109)
    c: InternalAlignment(g108,g109)
    c: InternalAlignment(g110,g109)
    c: InternalAlignment(g111,g109)
    c: Block(g103)
    c: Block(g109)
    c: Coincident(g112,g103)
    c: Coincident(g112,g109)
    c: Vertical(g112)
    c: Coincident(g113,g103)
    c: Coincident(g113,g64)
    c: Coincident(g114,g64)
    c: Coincident(g114,g109)
    c: Weight(g115) = 1
    c: Equal(g115,g116)
    c: Equal(g115,g117)
    c: InternalAlignment(g115,g118)
    c: InternalAlignment(g116,g118)
    c: InternalAlignment(g117,g118)
    c: InternalAlignment(g119,g118)
    c: InternalAlignment(g120,g118)
    c: Weight(g121) = 1
    c: Equal(g121,g122)
    c: Equal(g121,g123)
    c: InternalAlignment(g121,g124)
    c: InternalAlignment(g122,g124)
    c: InternalAlignment(g123,g124)
    c: InternalAlignment(g125,g124)
    c: InternalAlignment(g126,g124)
    c: Block(g118)
    c: Block(g124)
    c: Coincident(g127,g118)
    c: Coincident(g127,g124)
    c: Vertical(g127)
    c: Coincident(g128,g124)
    c: Coincident(g128,g82)
    c: Coincident(g129,g82)
    c: Coincident(g129,g118)
    c: Weight(g130) = 1
    c: Equal(g130,g131)
    c: Equal(g130,g132)
    c: InternalAlignment(g130,g133)
    c: InternalAlignment(g131,g133)
    c: InternalAlignment(g132,g133)
    c: InternalAlignment(g134,g133)
    c: InternalAlignment(g135,g133)
    c: Weight(g136) = 1
    c: Equal(g136,g137)
    c: Equal(g136,g138)
    c: InternalAlignment(g136,g139)
    c: InternalAlignment(g137,g139)
    c: InternalAlignment(g138,g139)
    c: InternalAlignment(g140,g139)
    c: InternalAlignment(g141,g139)
    c: Block(g133)
    c: Block(g139)
    c: Coincident(g142,g133)
    c: Coincident(g142,g139)
    c: Vertical(g142)
    c: Coincident(g143,g139)
    c: Coincident(g143,g76)
    c: Coincident(g144,g76)
    c: Coincident(g144,g133)
    c: Weight(g145) = 1
    c: Equal(g145,g146)
    c: Equal(g145,g147)
    c: InternalAlignment(g145,g148)
    c: InternalAlignment(g146,g148)
    c: InternalAlignment(g147,g148)
    c: InternalAlignment(g149,g148)
    c: InternalAlignment(g150,g148)
    c: Weight(g151) = 1
    c: Equal(g151,g152)
    c: Equal(g151,g153)
    c: InternalAlignment(g151,g154)
    c: InternalAlignment(g152,g154)
    c: InternalAlignment(g153,g154)
    c: InternalAlignment(g155,g154)
    c: InternalAlignment(g156,g154)
    c: Weight(g157) = 1
    c: Equal(g157,g158)
    c: Equal(g157,g159)
    c: InternalAlignment(g157,g160)
    c: InternalAlignment(g158,g160)
    c: InternalAlignment(g159,g160)
    c: InternalAlignment(g161,g160)
    c: InternalAlignment(g162,g160)
    c: Weight(g163) = 1
    c: Equal(g163,g164)
    c: Equal(g163,g165)
    c: InternalAlignment(g163,g166)
    c: InternalAlignment(g164,g166)
    c: InternalAlignment(g165,g166)
    c: InternalAlignment(g167,g166)
    c: InternalAlignment(g168,g166)
    c: Block(g166)
    c: Block(g160)
    c: Block(g154)
    c: Block(g148)
    c: Coincident(g169,g39)
    c: Coincident(g169,g166)
    c: Coincident(g170,g166)
    c: Coincident(g170,g160)
    c: Horizontal(g170)
    c: Coincident(g171,g160)
    c: Coincident(g171,g39)
    c: Vertical(g171)
    c: Coincident(g172,g33)
    c: Coincident(g172,g154)
    c: Vertical(g172)
    c: Coincident(g173,g154)
    c: Coincident(g173,g148)
    c: Horizontal(g173)
    c: Coincident(g174,g148)
    c: Coincident(g174,g33)
    c: Weight(g175) = 1
    c: Equal(g175,g176)
    c: Equal(g175,g177)
    c: InternalAlignment(g175,g178)
    c: InternalAlignment(g176,g178)
    c: InternalAlignment(g177,g178)
    c: InternalAlignment(g179,g178)
    c: InternalAlignment(g180,g178)
    c: Weight(g181) = 1
    c: Equal(g181,g182)
    c: Equal(g181,g183)
    c: InternalAlignment(g181,g184)
    c: InternalAlignment(g182,g184)
    c: InternalAlignment(g183,g184)
    c: InternalAlignment(g185,g184)
    c: InternalAlignment(g186,g184)
    c: Weight(g187) = 1
    c: Equal(g187,g188)
    c: Equal(g187,g189)
    c: InternalAlignment(g187,g190)
    c: InternalAlignment(g188,g190)
    c: InternalAlignment(g189,g190)
    c: InternalAlignment(g191,g190)
    c: InternalAlignment(g192,g190)
    c: Weight(g193) = 1
    c: Equal(g193,g194)
    c: Equal(g193,g195)
    c: InternalAlignment(g193,g196)
    c: InternalAlignment(g194,g196)
    c: InternalAlignment(g195,g196)
    c: InternalAlignment(g197,g196)
    c: InternalAlignment(g198,g196)
    c: Block(g196)
    c: Block(g190)
    c: Block(g184)
    c: Block(g178)
    c: Coincident(g199,g196)
    c: Coincident(g199,g190)
    c: Horizontal(g199)
    c: Coincident(g200,g190)
    c: Coincident(g200,g21)
    c: Vertical(g200)
    c: Coincident(g201,g27)
    c: Coincident(g201,g184)
    c: Vertical(g201)
    c: Coincident(g202,g184)
    c: Coincident(g202,g178)
    c: Horizontal(g202)
    c: Coincident(g203,g178)
    c: Coincident(g203,g27)
    c: Coincident(g204,g21)
    c: Weight(g205) = 1
    c: Equal(g205,g206)
    c: Equal(g205,g207)
    c: InternalAlignment(g205,g208)
    c: InternalAlignment(g206,g208)
    c: InternalAlignment(g207,g208)
    c: InternalAlignment(g209,g208)
    c: InternalAlignment(g210,g208)
    c: Weight(g211) = 1
    c: Equal(g211,g212)
    c: Equal(g211,g213)
    c: InternalAlignment(g211,g214)
    c: InternalAlignment(g212,g214)
    c: InternalAlignment(g213,g214)
    c: InternalAlignment(g215,g214)
    c: InternalAlignment(g216,g214)
    c: Block(g214)
    c: Block(g208)
    c: Coincident(g217,g214)
    c: Coincident(g217,g45)
    c: Coincident(g218,g45)
    c: Coincident(g218,g208)
    c: Coincident(g219,g208)
    c: Coincident(g219,g214)
    c: Vertical(g219)
    c: Weight(g220) = 1
    c: Equal(g220,g221)
    c: Equal(g220,g222)
    c: InternalAlignment(g220,g223)
    c: InternalAlignment(g221,g223)
    c: InternalAlignment(g222,g223)
    c: InternalAlignment(g224,g223)
    c: InternalAlignment(g225,g223)
    c: Weight(g226) = 1
    c: Equal(g226,g227)
    c: Equal(g226,g228)
    c: InternalAlignment(g226,g229)
    c: InternalAlignment(g227,g229)
    c: InternalAlignment(g228,g229)
    c: InternalAlignment(g230,g229)
    c: InternalAlignment(g231,g229)
    c: Block(g229)
    c: Block(g223)
    c: Coincident(g232,g223)
    c: Coincident(g232,g51)
    c: Coincident(g233,g51)
    c: Coincident(g233,g229)
    c: Coincident(g234,g229)
    c: Coincident(g234,g223)
    c: Vertical(g234)
    c: Horizontal(g235)
    c: Block(g235)
    c: Vertical(g236)
    c: Block(g236)
    c: Block(g237)
    c: Weight(g238) = 1
    c: Equal(g238,g239)
    c: Equal(g238,g240)
    c: InternalAlignment(g238,g241)
    c: InternalAlignment(g239,g241)
    c: InternalAlignment(g240,g241)
    c: InternalAlignment(g242,g241)
    c: InternalAlignment(g243,g241)
    c: Weight(g244) = 1
    c: Equal(g244,g245)
    c: Equal(g244,g246)
    c: InternalAlignment(g244,g247)
    c: InternalAlignment(g245,g247)
    c: InternalAlignment(g246,g247)
    c: InternalAlignment(g248,g247)
    c: InternalAlignment(g249,g247)
    c: Weight(g250) = 1
    c: Equal(g250,g251)
    c: Equal(g250,g252)
    c: InternalAlignment(g250,g253)
    c: InternalAlignment(g251,g253)
    c: InternalAlignment(g252,g253)
    c: InternalAlignment(g254,g253)
    c: InternalAlignment(g255,g253)
    c: Weight(g256) = 1
    c: Equal(g256,g257)
    c: Equal(g256,g258)
    c: InternalAlignment(g256,g259)
    c: InternalAlignment(g257,g259)
    c: InternalAlignment(g258,g259)
    c: InternalAlignment(g260,g259)
    c: InternalAlignment(g261,g259)
    c: Block(g241)
    c: Block(g247)
    c: Block(g253)
    c: Block(g259)
    c: Coincident(g262,g247)
    c: Coincident(g262,g241)
    c: Horizontal(g262)
    c: Block(g204)
    c: Weight(g263) = 1
    c: Equal(g263,g264)
    c: Equal(g263,g265)
    c: InternalAlignment(g263,g266)
    c: InternalAlignment(g264,g266)
    c: InternalAlignment(g265,g266)
    c: InternalAlignment(g267,g266)
    c: InternalAlignment(g268,g266)
    c: Weight(g269) = 1
    c: Equal(g269,g270)
    c: Equal(g269,g271)
    c: InternalAlignment(g269,g272)
    c: InternalAlignment(g270,g272)
    c: InternalAlignment(g271,g272)
    c: InternalAlignment(g273,g272)
    c: InternalAlignment(g274,g272)
    c: Weight(g275) = 1
    c: Equal(g275,g276)
    c: Equal(g275,g277)
    c: InternalAlignment(g275,g278)
    c: InternalAlignment(g276,g278)
    c: InternalAlignment(g277,g278)
    c: InternalAlignment(g279,g278)
    c: InternalAlignment(g280,g278)
    c: Weight(g281) = 1
    c: Equal(g281,g282)
    c: Equal(g281,g283)
    c: InternalAlignment(g281,g284)
    c: InternalAlignment(g282,g284)
    c: InternalAlignment(g283,g284)
    c: InternalAlignment(g285,g284)
    c: InternalAlignment(g286,g284)
    c: Block(g266)
    c: Block(g272)
    c: Block(g278)
    c: Block(g284)
    c: Coincident(g287,g278)
    c: Coincident(g287,g284)
    c: Horizontal(g287)
    c: Coincident(g288,g284)
    c: Coincident(g288,g266)
    c: Vertical(g288)
    c: Coincident(g289,g266)
    c: Coincident(g289,g272)
    c: Coincident(g290,g272)
    c: Coincident(g290,g278)
    c: Vertical(g290)
    c: Horizontal(g293)
    c: Horizontal(g294)
    c: Vertical(g295)
    c: Vertical(g296)
    c: Distance(g296) = 4
    c: Distance(g291) = 4
    c: Distance(g295) = 4
    c: Distance(g294) = 4
    c: Distance(g293) = 4
    c: Distance(g292) = 4
    c: Coincident(g297,g3)
    c: Coincident(g297,g4)
    c: Parallel(g292,g297)
    c: Coincident(g292,g4)
    c: Coincident(g293,g4)
    c: Coincident(g294,g3)
    c: Coincident(g295,g3)
    c: Coincident(g296,g3)
    c: Coincident(g291,g3)
FEATURE [Sketcher::SketchObject] Sketch001
  FullyConstrained = true
  MapMode = 4
  Placement = pos=(0,0,0) rot=(0.57735,0.57735,0.57735;2.0944rad)
  Support = -> [Sketch]
  sketch-geometry (46):
    g0: BSplineCurve PolesCount=3 KnotsCount=2 Degree=2 IsPeriodic=0
    g1: ArcOfCircle CenterX=73.1223 CenterY=-32.291 CenterZ=0 NormalX=0 NormalY=0 NormalZ=1 AngleXU=0 Radius=13 StartAngle=5.92268 EndAngle=9.06428
    g2: ArcOfCircle CenterX=66.7816 CenterY=-49.1439 CenterZ=0 NormalX=0 NormalY=0 NormalZ=1 AngleXU=0 Radius=13 StartAngle=2.78068 EndAngle=5.92131
    g3: ArcOfCircle CenterX=55.9263 CenterY=-78.1807 CenterZ=0 NormalX=0 NormalY=0 NormalZ=1 AngleXU=0 Radius=13 StartAngle=5.92268 EndAngle=9.06428
    g4: ArcOfCircle CenterX=49.5884 CenterY=-95.0342 CenterZ=0 NormalX=0 NormalY=0 NormalZ=1 AngleXU=0 Radius=13 StartAngle=2.78068 EndAngle=5.92131
    g5: ArcOfCircle CenterX=38.7206 CenterY=-124.067 CenterZ=0 NormalX=0 NormalY=0 NormalZ=1 AngleXU=0 Radius=13 StartAngle=5.92268 EndAngle=9.06428
    g6: ArcOfCircle CenterX=32.3875 CenterY=-140.92 CenterZ=0 NormalX=0 NormalY=0 NormalZ=1 AngleXU=0 Radius=13 StartAngle=2.78068 EndAngle=5.92131
    g7: ArcOfCircle CenterX=21.4715 CenterY=-169.934 CenterZ=0 NormalX=0 NormalY=0 NormalZ=1 AngleXU=0 Radius=13 StartAngle=5.92268 EndAngle=9.06428
    g8: ArcOfCircle CenterX=15.1336 CenterY=-186.787 CenterZ=0 NormalX=0 NormalY=0 NormalZ=1 AngleXU=0 Radius=13 StartAngle=2.78068 EndAngle=5.92131
    g9-g12: Circle x4 (B-spline internal-alignment scaffolding for g13; pole/knot coordinates omitted)
    g13: BSplineCurve PolesCount=4 KnotsCount=2 Degree=3 IsPeriodic=0
    g14: GeomPoint X=28.8094 Y=-19.0875 Z=0
    g15: GeomPoint X=47.0443 Y=-50.4712 Z=0
    g16: Circle CenterX=53.5586 CenterY=-23.2695 CenterZ=0 NormalX=0 NormalY=0 NormalZ=1 AngleXU=0 Radius=3.24518
    g17: Circle CenterX=-195.441 CenterY=-127.082 CenterZ=0 NormalX=0 NormalY=0 NormalZ=1 AngleXU=0 Radius=1
    g18: Circle CenterX=-8.24091 CenterY=-197.481 CenterZ=0 NormalX=0 NormalY=0 NormalZ=1 AngleXU=0 Radius=1
    g19: Circle CenterX=12.8789 CenterY=-141.321 CenterZ=0 NormalX=0 NormalY=0 NormalZ=1 AngleXU=0 Radius=1
    g20: BSplineCurve PolesCount=3 KnotsCount=2 Degree=2 IsPeriodic=0
    g21: GeomPoint X=-195.441 Y=-127.082 Z=0
    g22: GeomPoint X=12.8789 Y=-141.321 Z=0
    g23: Circle CenterX=-12.8016 CenterY=-179.036 CenterZ=0 NormalX=0 NormalY=0 NormalZ=1 AngleXU=0 Radius=10.5072
    g24: Circle CenterX=0.933922 CenterY=-166.43 CenterZ=0 NormalX=0 NormalY=0 NormalZ=1 AngleXU=0 Radius=3.26661
    g25: Circle CenterX=-33.5518 CenterY=-176.44 CenterZ=0 NormalX=0 NormalY=0 NormalZ=1 AngleXU=0 Radius=5.64388
    g26: Circle CenterX=-47.2366 CenterY=-173.859 CenterZ=0 NormalX=0 NormalY=0 NormalZ=1 AngleXU=0 Radius=3.01653
    g27: Circle CenterX=-56.2595 CenterY=-171.456 CenterZ=0 NormalX=0 NormalY=0 NormalZ=1 AngleXU=0 Radius=2.12826
    g28: ArcOfCircle CenterX=51.2151 CenterY=-198.473 CenterZ=0 NormalX=0 NormalY=0 NormalZ=1 AngleXU=0 Radius=20 StartAngle=2.78189 EndAngle=4.35269
    g29: LineSegment StartX=32.4951 StartY=-191.433 StartZ=0 EndX=94.6578 EndY=-26.1352 EndZ=0
    g30: LineSegment StartX=43.1192 StartY=-220.001 StartZ=0 EndX=-196.497 EndY=-129.89 EndZ=0
    g31: LineSegment StartX=43.1192 StartY=-220.001 StartZ=0 EndX=44.1752 EndY=-217.193 EndZ=0
    g32: LineSegment StartX=117.223 StartY=-19.0875 StartZ=0 EndX=117.223 EndY=-16.0875 EndZ=0
    g33: LineSegment StartX=117.223 StartY=-16.0875 StartZ=0 EndX=17.2232 EndY=-16.0875 EndZ=0
    g34: LineSegment StartX=17.2232 StartY=-16.0875 StartZ=0 EndX=17.2232 EndY=-19.0875 EndZ=0
    g35: LineSegment StartX=28.8094 StartY=-19.0875 StartZ=0 EndX=17.2232 EndY=-19.0875 EndZ=0
    g36: LineSegment StartX=47.0443 StartY=-50.4712 StartZ=0 EndX=12.8789 EndY=-141.321 EndZ=0
    g37: LineSegment StartX=-195.441 StartY=-127.082 StartZ=0 EndX=-196.497 EndY=-129.89 EndZ=0
    g38: LineSegment StartX=85.2866 StartY=-36.8766 StartZ=0 EndX=78.9396 EndY=-53.7463 EndZ=0
    g39: LineSegment StartX=60.9579 StartY=-27.7053 StartZ=0 EndX=54.6191 EndY=-44.5532 EndZ=0
    g40: LineSegment StartX=68.0907 StartY=-82.7664 StartZ=0 EndX=61.7465 EndY=-99.6365 EndZ=0
    g41: LineSegment StartX=43.7619 StartY=-73.595 StartZ=0 EndX=37.426 EndY=-90.4435 EndZ=0
    g42: LineSegment StartX=50.885 StartY=-128.652 StartZ=0 EndX=44.5456 EndY=-145.522 EndZ=0
    g43: LineSegment StartX=26.5562 StartY=-119.481 StartZ=0 EndX=20.2251 EndY=-136.329 EndZ=0
    g44: LineSegment StartX=9.3071 StartY=-165.349 StartZ=0 EndX=2.97115 EndY=-182.197 EndZ=0
    g45: LineSegment StartX=33.6358 StartY=-174.52 StartZ=0 EndX=27.2917 EndY=-191.39 EndZ=0
  constraints (71):
    c: Block(g0)
    c: Block(g1)
    c: Block(g2)
    c: Block(g4)
    c: Block(g3)
    c: Block(g6)
    c: Block(g5)
    c: Block(g8)
    c: Block(g7)
    c: Weight(g9) = 1
    c: Equal(g9,g10)
    c: Equal(g9,g11)
    c: Equal(g9,g12)
    c: InternalAlignment(g9-g12 -> g13) x4
    c: InternalAlignment(g14,g13)
    c: InternalAlignment(g15,g13)
    c: Block(g16)
    c: Weight(g17) = 1
    c: Equal(g17,g18)
    c: Equal(g17,g19)
    c: InternalAlignment(g17,g20)
    c: InternalAlignment(g18,g20)
    c: InternalAlignment(g19,g20)
    c: InternalAlignment(g21,g20)
    c: InternalAlignment(g22,g20)
    c: Block(g20)
    c: Block(g23)
    c: Block(g24)
    c: Block(g25)
    c: Block(g26)
    c: Block(g27)
    c: Block(g28)
    c: Coincident(g29,g28)
    c: Coincident(g29,g0)
    c: Block(g13)
    c: Coincident(g31,g30)
    c: Coincident(g31,g28)
    c: Block(g31)
    c: Coincident(g32,g0)
    c: Vertical(g32)
    c: Coincident(g33,g32)
    c: Horizontal(g33)
    c: Coincident(g34,g33)
    c: Vertical(g34)
    c: Block(g33)
    c: Coincident(g35,g13)
    c: Coincident(g35,g34)
    c: Horizontal(g35)
    c: Coincident(g36,g13)
    c: Coincident(g36,g20)
    c: Coincident(g37,g20)
    c: Coincident(g37,g30)
    c: Block(g30)
    c: Coincident(g38,g1)
    c: Coincident(g38,g2)
    c: Coincident(g39,g1)
    c: Coincident(g39,g2)
    c: Coincident(g40,g3)
    c: Coincident(g40,g4)
    c: Coincident(g41,g3)
    c: Coincident(g41,g4)
    c: Coincident(g42,g5)
    c: Coincident(g42,g6)
    c: Coincident(g43,g5)
    c: Coincident(g43,g6)
    c: Coincident(g44,g7)
    c: Coincident(g44,g8)
    c: Coincident(g45,g7)
    c: Coincident(g45,g8)
    c: Distance(g30) = 256
    c: Distance(g33) = 100
FEATURE [Part::Extrusion] Extrude002
  Base = -> Sketch001
  Dir = (1,0,0)
  DirMode = 2
  FaceMakerClass = Part::FaceMakerBullseye
  LengthFwd = 8
  LengthRev = 0
  Solid = true
  Symmetric = false
FEATURE [Sketcher::SketchObject] Sketch002
  FullyConstrained = true
  sketch-geometry (20):
    g0: LineSegment StartX=-2.77179 StartY=-200.304 StartZ=0 EndX=5.22821 EndY=-200.304 EndZ=0
    g1: LineSegment StartX=5.22821 StartY=-200.304 StartZ=0 EndX=5.22821 EndY=-197.304 EndZ=0
    g2: LineSegment StartX=-2.77179 StartY=-200.304 StartZ=0 EndX=-2.77179 EndY=-197.304 EndZ=0
    g3: LineSegment StartX=5.22821 StartY=-197.304 StartZ=0 EndX=8.22821 EndY=-197.304 EndZ=0
    g4: LineSegment StartX=-2.77179 StartY=-197.304 StartZ=0 EndX=-5.77179 EndY=-197.304 EndZ=0
    g5: LineSegment StartX=19.2282 StartY=-203.304 StartZ=0 EndX=19.2282 EndY=-206.304 EndZ=0
    g6: LineSegment StartX=-16.7718 StartY=-203.304 StartZ=0 EndX=-16.7718 EndY=-206.304 EndZ=0
    g7: LineSegment StartX=-16.7718 StartY=-206.304 StartZ=0 EndX=19.2282 EndY=-206.304 EndZ=0
    g8: Circle CenterX=-16.7718 CenterY=-203.304 CenterZ=0 NormalX=0 NormalY=0 NormalZ=1 AngleXU=0 Radius=1
    g9: Circle CenterX=-5.77179 CenterY=-203.304 CenterZ=0 NormalX=0 NormalY=0 NormalZ=1 AngleXU=0 Radius=1
    g10: Circle CenterX=-5.77179 CenterY=-197.304 CenterZ=0 NormalX=0 NormalY=0 NormalZ=1 AngleXU=0 Radius=1
    g11: BSplineCurve PolesCount=3 KnotsCount=2 Degree=2 IsPeriodic=0
    g12: GeomPoint X=-16.7718 Y=-203.304 Z=0
    g13: GeomPoint X=-5.77179 Y=-197.304 Z=0
    g14: Circle CenterX=19.2282 CenterY=-203.304 CenterZ=0 NormalX=0 NormalY=0 NormalZ=1 AngleXU=0 Radius=1
    g15: Circle CenterX=8.22821 CenterY=-203.304 CenterZ=0 NormalX=0 NormalY=0 NormalZ=1 AngleXU=0 Radius=1
    g16: Circle CenterX=8.22821 CenterY=-197.304 CenterZ=0 NormalX=0 NormalY=0 NormalZ=1 AngleXU=0 Radius=1
    g17: BSplineCurve PolesCount=3 KnotsCount=2 Degree=2 IsPeriodic=0
    g18: GeomPoint X=19.2282 Y=-203.304 Z=0
    g19: GeomPoint X=8.22821 Y=-197.304 Z=0
  constraints (41):
    c: Horizontal(g0)
    c: Distance(g0) = 8
    c: Coincident(g1,g0)
    c: Vertical(g1)
    c: Distance(g1) = 3
    c: Coincident(g2,g0)
    c: Vertical(g2)
    c: Distance(g2) = 3
    c: Coincident(g3,g1)
    c: Horizontal(g3)
    c: Distance(g3) = 3
    c: Coincident(g4,g2)
    c: Horizontal(g4)
    c: Distance(g4) = 3
    c: Vertical(g5)
    c: Vertical(g6)
    c: Coincident(g7,g6)
    c: Coincident(g7,g5)
    c: Weight(g8) = 1
    c: Equal(g8,g9)
    c: Equal(g8,g10)
    c: Coincident(g11,g4)
    c: InternalAlignment(g8,g11)
    c: InternalAlignment(g9,g11)
    c: InternalAlignment(g10,g11)
    c: InternalAlignment(g12,g11)
    c: InternalAlignment(g13,g11)
    c: Coincident(g17,g5)
    c: Weight(g14) = 1
    c: Equal(g14,g15)
    c: Equal(g14,g16)
    c: Coincident(g17,g3)
    c: InternalAlignment(g14,g17)
    c: InternalAlignment(g15,g17)
    c: InternalAlignment(g16,g17)
    c: InternalAlignment(g18,g17)
    c: InternalAlignment(g19,g17)
    c: Block(g7)
    c: Block(g17)
    c: Block(g11)
    c: Block(g6)
FEATURE [Part::Extrusion] Extrude003
  Base = -> Sketch002
  Dir = (0,0,1)
  DirMode = 2
  FaceMakerClass = Part::FaceMakerBullseye
  LengthFwd = 260
  LengthRev = 0
  Solid = true
  Symmetric = false
FEATURE [Part::Extrusion] Extrude
  Base = -> Sketch
  Dir = (0,0,1)
  DirMode = 2
  FaceMakerClass = Part::FaceMakerBullseye
  LengthFwd = 14
  LengthRev = 0
  Solid = true
  Symmetric = false
